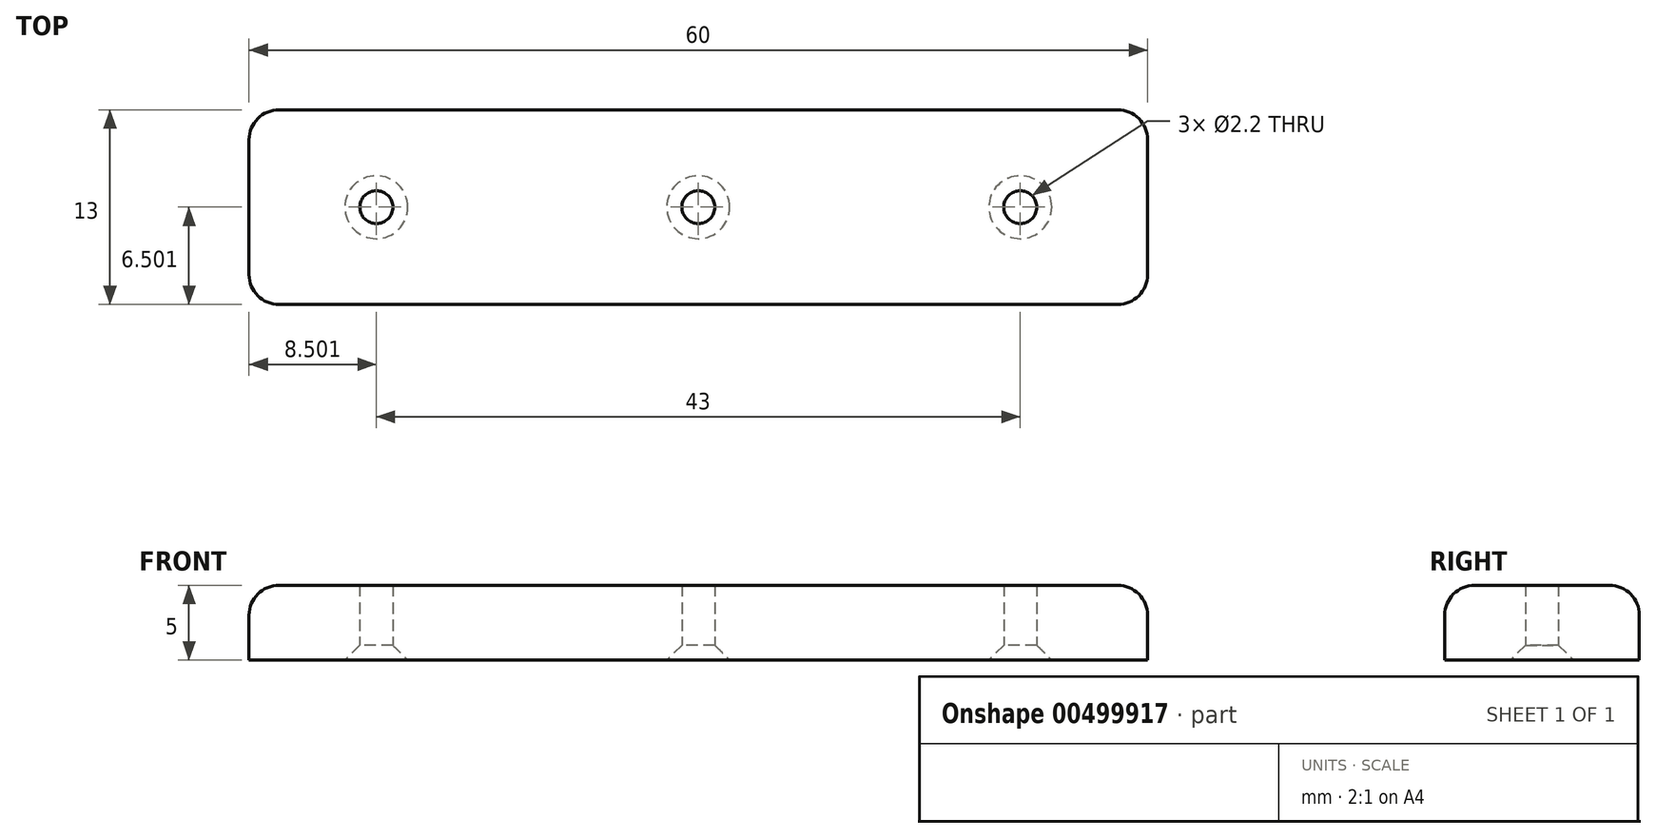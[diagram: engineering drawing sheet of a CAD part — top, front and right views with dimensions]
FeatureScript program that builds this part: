
annotation { "Feature Type Name" : "Feature", "Feature Type Description" : "" }
export const myFeature = defineFeature(function(context is Context, id is Id, definition is map)
    precondition{}
    {
        {
            var Q0;
            Q0=qCreatedBy(makeId("Top.planeOp"),FACE);
            var sketch = newSketch(context, id + "F0", { "sketchPlane" : qUnion([Q0])});
            skLineSegment(sketch, "E0.bottom", {"start": v(-34.23, 3.76) * mm, "end": v(25.77, 3.76) * mm});
            skLineSegment(sketch, "E0.top", {"start": v(-34.23, -9.24) * mm, "end": v(25.77, -9.24) * mm});
            skLineSegment(sketch, "E0.left", {"start": v(-34.23, 3.76) * mm, "end": v(-34.23, -9.24) * mm});
            skLineSegment(sketch, "E0.right", {"start": v(25.77, 3.76) * mm, "end": v(25.77, -9.24) * mm});
            skCircle(sketch, "E1", {"center": v(-25.73, -2.74) * mm, "radius": 1.1 * mm});
            skCircle(sketch, "E2.1.0.0", {"center": v(-4.23, -2.74) * mm, "radius": 1.1 * mm});
            skCircle(sketch, "E2.2.0.0", {"center": v(17.27, -2.74) * mm, "radius": 1.1 * mm});
            skLineSegment(sketch, "E2.direction1", {"start": v(-25.73, -2.74) * mm, "end": v(-4.23, -2.74) * mm, "construction": true});
            skSolve(sketch);
        }
        {
            var Q0;
            Q0 = qSketchRegion(id + "F0", true);
            extrude(context, id + "F1", {"entities" : qUnion([Q0]), "depth" : 5 * mm});
        }
        {
            var Q0;
            Q0=makeQuery(id+"F1.opExtrude","CAP_EDGE",EDGE,{"disambiguationData":[OSD([sQuery(id+"F0.wireOp",EDGE,"E0.top")])],"isStart":false});
            var Q1;
            Q1=makeQuery(id+"F1.opExtrude","CAP_EDGE",EDGE,{"disambiguationData":[OSD([sQuery(id+"F0.wireOp",EDGE,"E0.right")])],"isStart":false});
            var Q2;
            Q2=makeQuery(id+"F1.opExtrude","SWEPT_EDGE",EDGE,{"disambiguationData":[OSD([sQuery(id+"F0.wireOp",EDGE,"E0.top"),sQuery(id+"F0.wireOp",EDGE,"E0.right")])]});
            var Q3;
            Q3=makeQuery(id+"F1.opExtrude","CAP_EDGE",EDGE,{"disambiguationData":[OSD([sQuery(id+"F0.wireOp",EDGE,"E0.bottom")])],"isStart":false});
            var Q4;
            Q4=makeQuery(id+"F1.opExtrude","CAP_EDGE",EDGE,{"disambiguationData":[OSD([sQuery(id+"F0.wireOp",EDGE,"E0.left")])],"isStart":false});
            var Q5;
            Q5=makeQuery(id+"F1.opExtrude","SWEPT_EDGE",EDGE,{"disambiguationData":[OSD([sQuery(id+"F0.wireOp",EDGE,"E0.top"),sQuery(id+"F0.wireOp",EDGE,"E0.left")])]});
            var Q6;
            Q6=makeQuery(id+"F1.opExtrude","SWEPT_EDGE",EDGE,{"disambiguationData":[OSD([sQuery(id+"F0.wireOp",EDGE,"E0.bottom"),sQuery(id+"F0.wireOp",EDGE,"E0.right")])]});
            var Q7;
            Q7=makeQuery(id+"F1.opExtrude","SWEPT_EDGE",EDGE,{"disambiguationData":[OSD([sQuery(id+"F0.wireOp",EDGE,"E0.bottom"),sQuery(id+"F0.wireOp",EDGE,"E0.left")])]});
            fillet(context, id + "F2", {"entities" : qUnion([Q0, Q1, Q2, Q3, Q4, Q5, Q6, Q7]), "radius" : 2 * mm, "tangentPropagation" : true, "allowEdgeOverflow" : false});
        }
        {
            var Q0;
            Q0=makeQuery(id+"F1.opExtrude","CAP_EDGE",EDGE,{"disambiguationData":[OSD([sQuery(id+"F0.wireOp",EDGE,"E2.1.0.0")])],"isStart":true});
            var Q1;
            Q1=makeQuery(id+"F1.opExtrude","CAP_EDGE",EDGE,{"disambiguationData":[OSD([sQuery(id+"F0.wireOp",EDGE,"E2.2.0.0")])],"isStart":true});
            var Q2;
            Q2=makeQuery(id+"F1.opExtrude","CAP_EDGE",EDGE,{"disambiguationData":[OSD([sQuery(id+"F0.wireOp",EDGE,"E1")])],"isStart":true});
            chamfer(context, id + "F3", {"entities" : qUnion([Q0, Q1, Q2]), "width" : 1 * mm, "tangentPropagation" : true});
        }
    });
